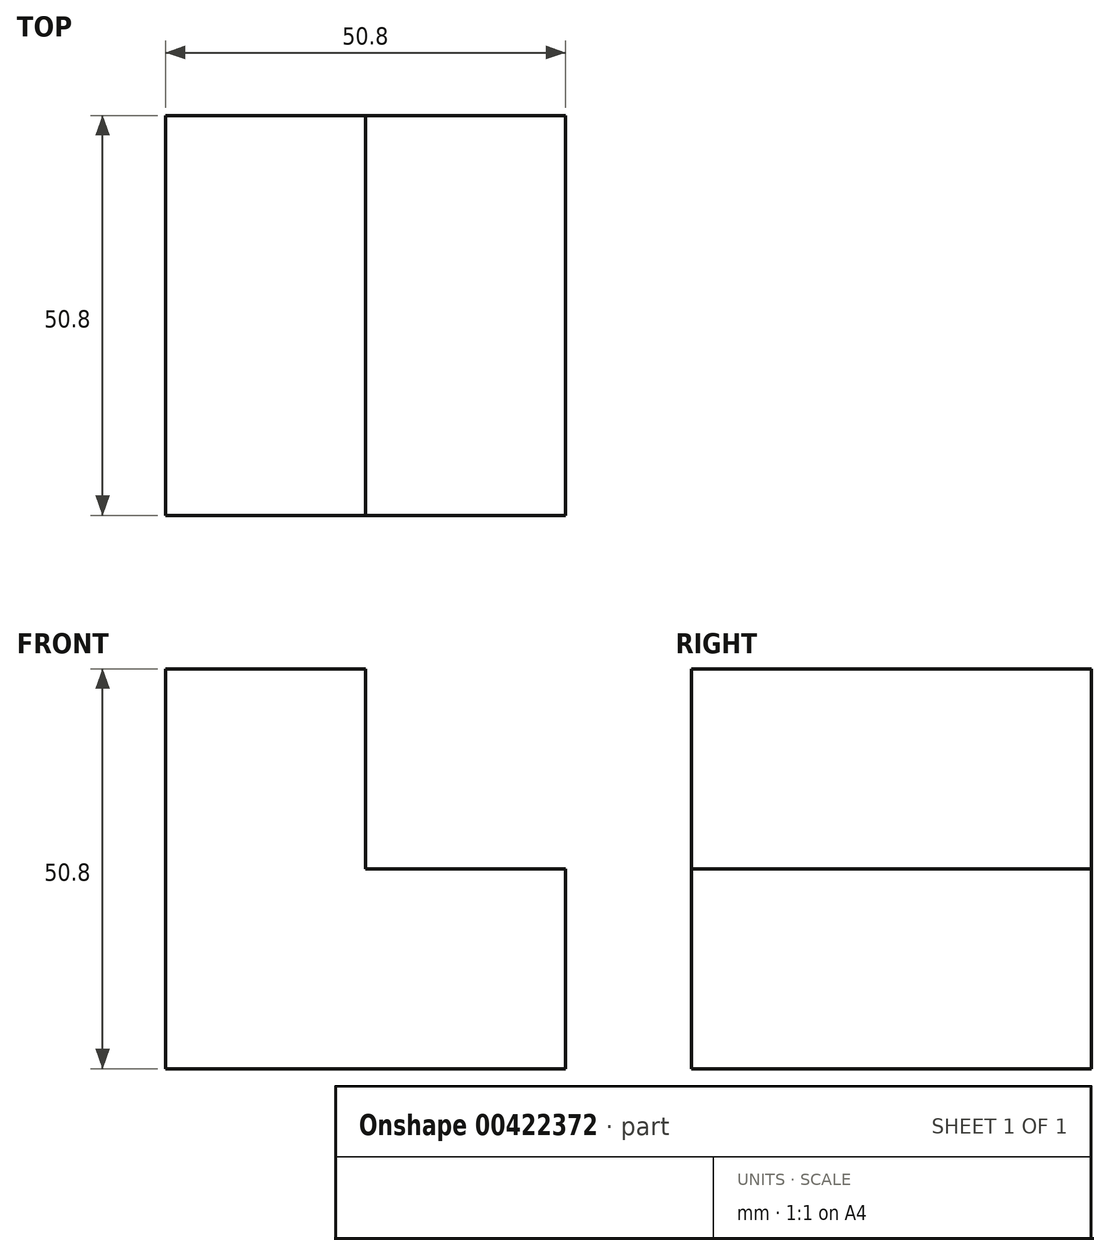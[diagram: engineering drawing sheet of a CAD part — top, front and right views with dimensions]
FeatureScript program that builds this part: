
annotation { "Feature Type Name" : "Feature", "Feature Type Description" : "" }
export const myFeature = defineFeature(function(context is Context, id is Id, definition is map)
    precondition{}
    {
        {
            var Q0;
            Q0=qCreatedBy(makeId("Front.planeOp"),FACE);
            var sketch = newSketch(context, id + "F0", { "sketchPlane" : qUnion([Q0])});
            skLineSegment(sketch, "E0", {"start": v(-38.75, 25.4) * mm, "end": v(-38.75, -25.4) * mm});
            skLineSegment(sketch, "E1", {"start": v(-38.75, 25.4) * mm, "end": v(-13.35, 25.4) * mm});
            skLineSegment(sketch, "E2", {"start": v(-13.35, 25.4) * mm, "end": v(-13.35, 0) * mm});
            skLineSegment(sketch, "E3", {"start": v(-13.35, 0) * mm, "end": v(12.05, 0) * mm});
            skLineSegment(sketch, "E4", {"start": v(12.05, 0) * mm, "end": v(12.05, -25.4) * mm});
            skLineSegment(sketch, "E5", {"start": v(12.05, -25.4) * mm, "end": v(-38.75, -25.4) * mm});
            skSolve(sketch);
        }
        {
            var Q0;
            Q0=makeQuery(id+"F0.imprint","IMPRINT",FACE,{"disambiguationData":[TD([[makeQuery(id+"F0.imprint","IMPRINT",EDGE,{"derivedFrom":sQuery(id+"F0.wireOp",EDGE,"E0")}),1.0]])]});
            extrude(context, id + "F1", {"entities" : qUnion([Q0]), "depth" : 50.8 * mm});
        }
    });
